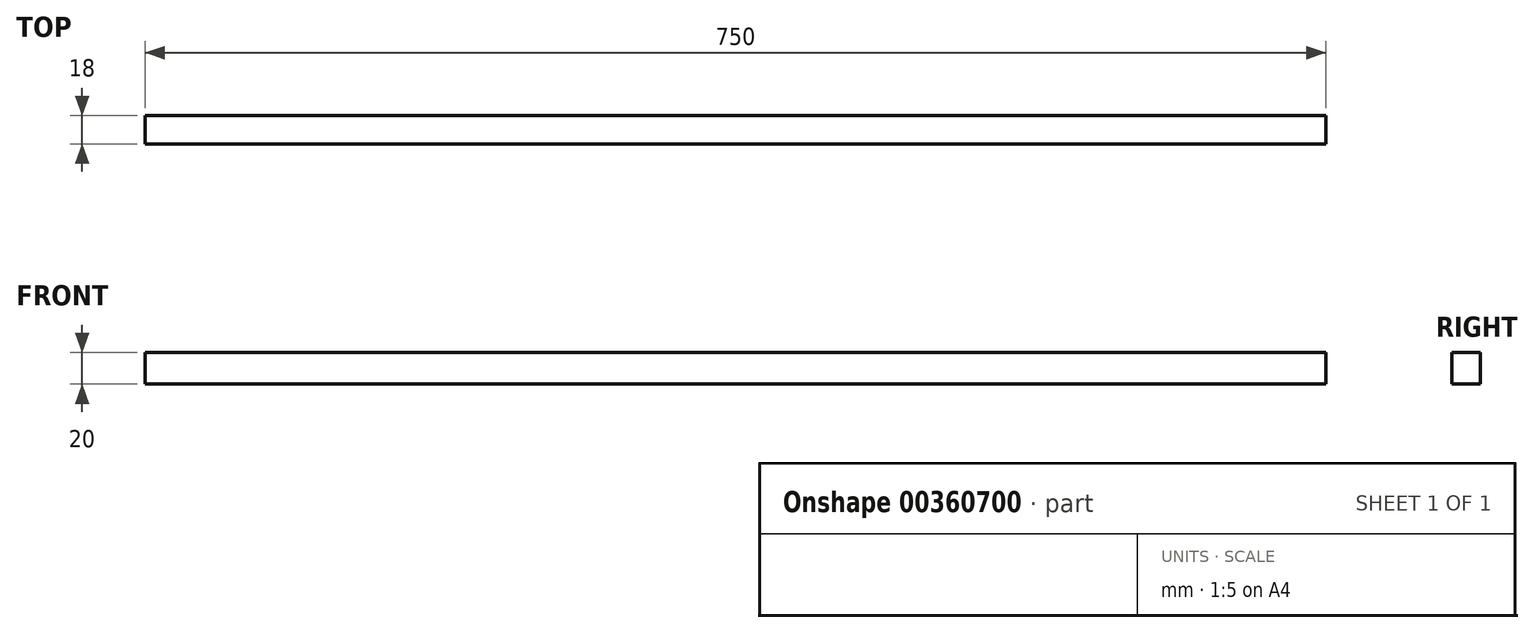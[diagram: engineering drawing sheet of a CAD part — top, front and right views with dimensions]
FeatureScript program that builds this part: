
annotation { "Feature Type Name" : "Feature", "Feature Type Description" : "" }
export const myFeature = defineFeature(function(context is Context, id is Id, definition is map)
    precondition{}
    {
        {
            var Q0;
            Q0=qCreatedBy(makeId("Front.planeOp"),FACE);
            var sketch = newSketch(context, id + "F0", { "sketchPlane" : qUnion([Q0])});
            skLineSegment(sketch, "E0.bottom", {"start": v(0, 0) * mm, "end": v(750, 0) * mm});
            skLineSegment(sketch, "E0.top", {"start": v(0, 20) * mm, "end": v(750, 20) * mm});
            skLineSegment(sketch, "E0.left", {"start": v(0, 0) * mm, "end": v(0, 20) * mm});
            skLineSegment(sketch, "E0.right", {"start": v(750, 0) * mm, "end": v(750, 20) * mm});
            skSolve(sketch);
        }
        {
            var Q0;
            Q0=makeQuery(id+"F0.imprint","IMPRINT",FACE,{"disambiguationData":[TD([[makeQuery(id+"F0.imprint","IMPRINT",EDGE,{"derivedFrom":sQuery(id+"F0.wireOp",EDGE,"E0.bottom")}),1.0]])]});
            extrude(context, id + "F1", {"entities" : qUnion([Q0]), "depth" : 18 * mm});
        }
    });
